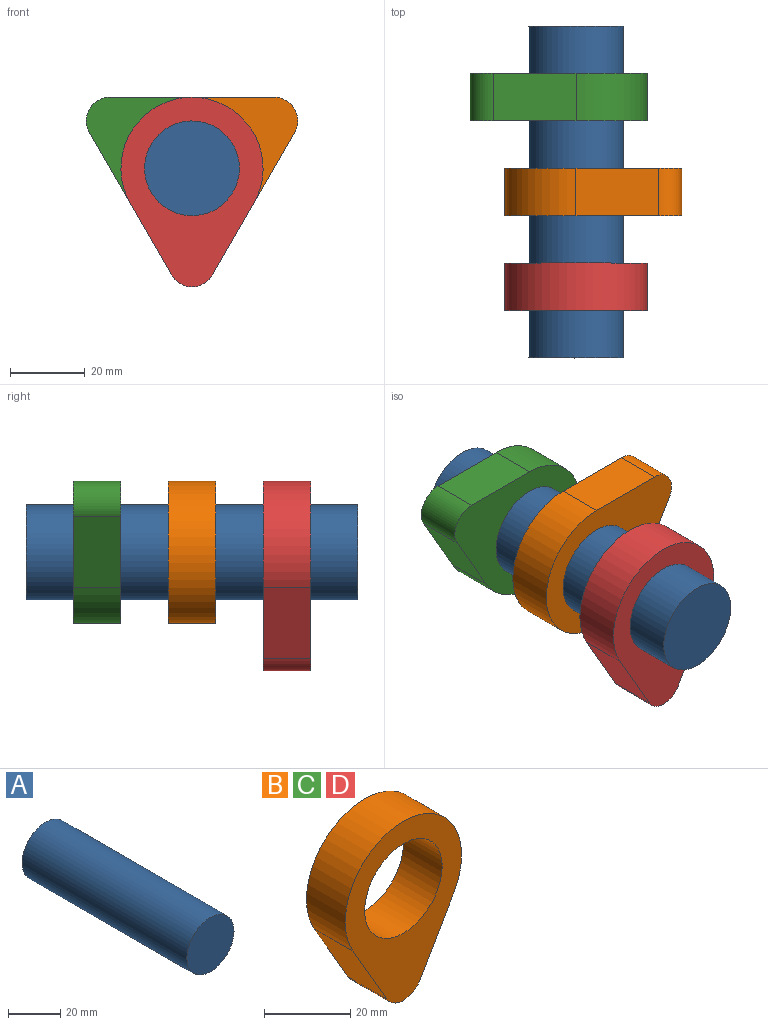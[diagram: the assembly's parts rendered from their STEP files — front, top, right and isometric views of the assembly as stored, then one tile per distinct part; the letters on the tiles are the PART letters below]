
ASSEMBLY  parts=4 mates=6
PART A: 3 faces, bbox 25.4x88.9x25.4 mm
  f0: cylinder r=12.7mm len=88.9mm, axis (0,1,0), area 7093.9mm2, adj f1,f2
  f1: plane 25.4x25.4mm, normal (0,-1,0), area 506.7mm2, adj f0
  f2: plane 25.4x25.4mm, normal (0,1,0), area 506.7mm2, adj f0
PART B: 7 faces, bbox 38.1x12.7x50.8 mm
  f0: plane 19.05x12.7mm, normal (0.87,0,-0.5), area 279.4mm2, adj f1,f3,f5,f6
  f1: cylinder r=19.05mm len=38.1mm, axis (0,1,0), area 1013.4mm2, adj f0,f2,f5,f6
  f2: plane 19.05x12.7mm, normal (-0.87,0,-0.5), area 279.4mm2, adj f1,f3,f5,f6
  f3: cylinder r=6.35mm len=12.7mm, axis (0,1,0), area 168.9mm2, adj f0,f2,f5,f6
  f4: cylinder r=12.7mm len=25.4mm, axis (0,1,0), area 1013.4mm2, adj f5,f6
  f5: plane 50.8x38.1mm, normal (0,-1,0), area 854.3mm2, adj f0,f1,f2,f3,f4
  f6: plane 50.8x38.1mm, normal (0,1,0), area 854.3mm2, adj f0,f1,f2,f3,f4
PART C: same geometry as B
PART D: same geometry as B
PLACE A t=(-17.5,15.84,-8.7)mm fixed
PLACE B rot(axis=(0,-1,0),120deg) t=(-17.5,-9.56,-8.7)mm
PLACE C rot(axis=(0,1,0),120deg) t=(-17.5,15.84,-8.7)mm
PLACE D t=(-17.5,-34.96,-8.7)mm
MATE cylindrical C.f1 <-> A.f0  axis (0,1,0) through (-17.5,15.84,-8.7)mm
MATE cylindrical D.f1 <-> A.f0  axis (0,-1,0) through (-17.5,-47.66,-8.7)mm
MATE pin_slot B.f1 <-> A.f0  axis (0,-1,0) through (-17.5,-22.26,-8.7)mm
MATE slider A.f0 <-> D.f1  axis (0,-1,0) through (-17.5,-60.36,-8.7)mm
MATE cylindrical B.f1 <-> A.f0  axis (0,-1,0) through (-17.5,-22.26,-8.7)mm
MATE pin_slot C.f1 <-> A.f0  axis (0,1,0) through (-17.5,3.14,-8.7)mm
